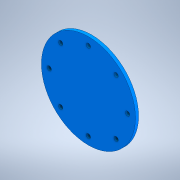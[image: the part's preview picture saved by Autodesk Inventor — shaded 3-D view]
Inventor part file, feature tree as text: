
AUTODESK INVENTOR PART (.ipt)
format: ipt  version: 2021 (Build 250183000, 183)  size: 141,312 bytes
history: native  units: mm
features: other x1, sketch x1, extrude x1
ambient origin geometry x8: Origin, YZ Plane, XZ Plane, XY Plane, X Axis, Y Axis, Z Axis, Center Point
bodies: Body1 (feature_tree)
feature tree (3):
  other  "Sólido1"
  sketch  "Boceto1"  dims[d0=120.0mm d1=5.5mm d2=5.5mm d3=5.5mm d4=5.5mm d5=5.5mm d6=5.5mm d7=5.5mm d8=5.5mm d9=50.0mm d10=7.25mm d11=50.0mm d12=50.0mm d13=50.0mm d14=50.0mm d15=50.0mm d16=50.0mm d17=50.0mm d19=4.0mm d20=0.0mm d21=90.0mm]
  extrude  "Extrusión1"  Depth=4.0mm TaperAngle=0.0deg
